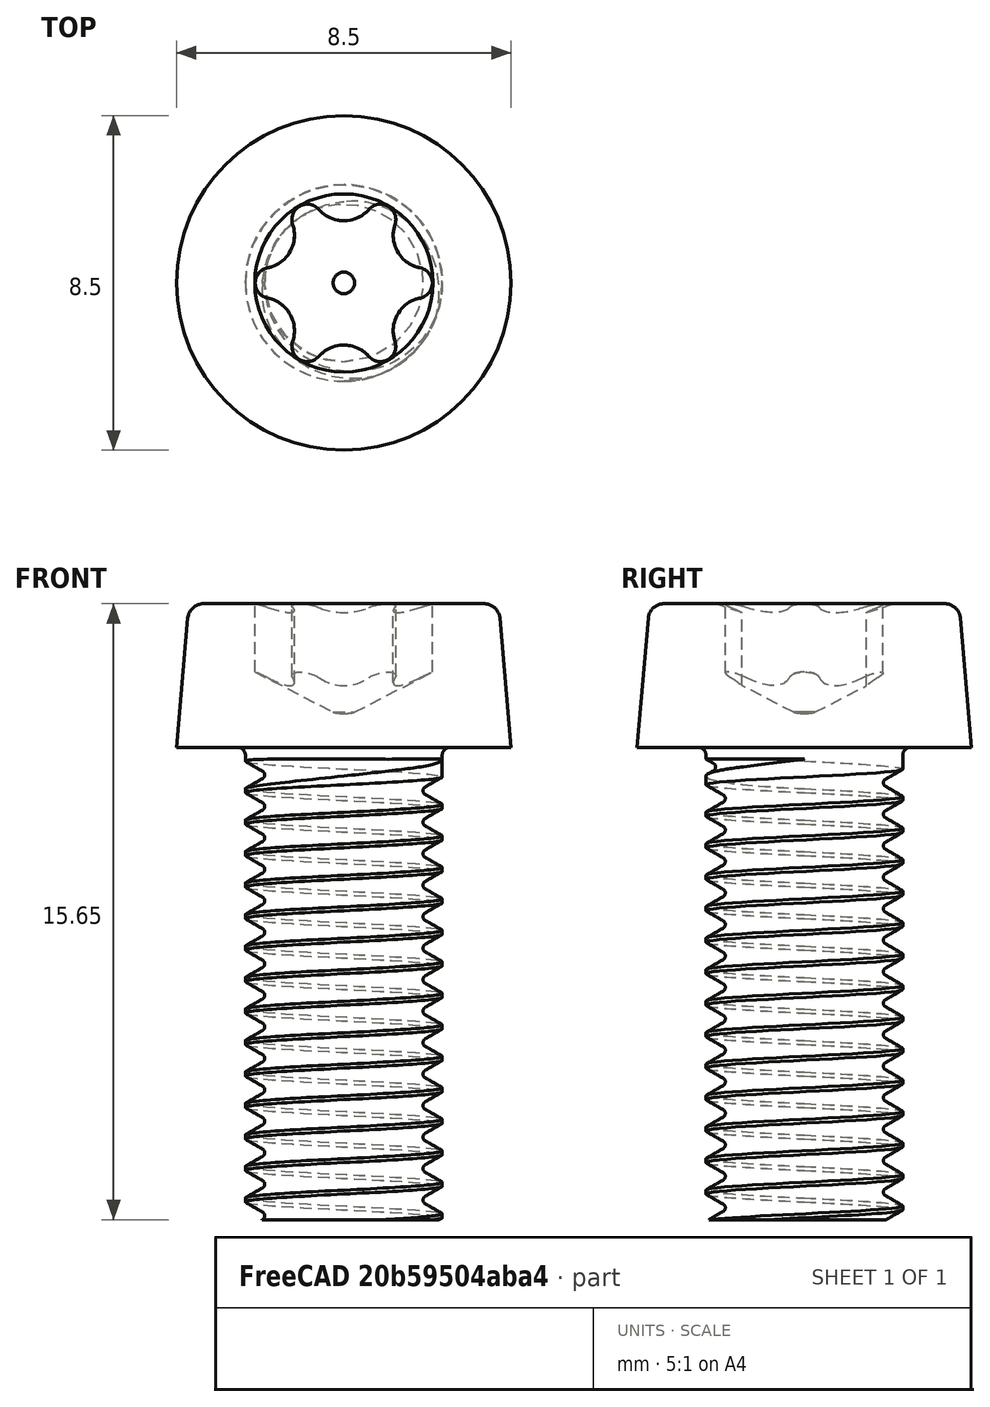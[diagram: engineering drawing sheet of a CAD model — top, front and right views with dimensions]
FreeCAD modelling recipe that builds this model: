
FCSTD DOCUMENT  (FreeCAD 0.20R29410 (Git))
Label: Assembly
License: All rights reserved
LicenseURL: http://en.wikipedia.org/wiki/All_rights_reserved
objects: App::DocumentObjectGroup×3, App::Link×3, Part::FeaturePython×2, PartDesign::CoordinateSystem×1, App::FeaturePython×1, App::Part×1
note: 3 computed .brp shape members not serialized (recipe doc carries the construction recipe); baked Part::Feature solids carry a one-line shape summary decoded from their .brp
EXTERNAL_REF file=Clip.FCStd obj=LCS_Origin
EXTERNAL_REF file=Clip.FCStd obj=Body
EXTERNAL_REF file=Clip.FCStd obj=HoleAxis_1
EXTERNAL_REF file=Rectangle.FCStd obj=HoleAxis_1
EXTERNAL_REF file=Rectangle.FCStd obj=Part

FEATURE [App::DocumentObjectGroup] Parts
FEATURE [PartDesign::CoordinateSystem] LCS_Origin
  AttacherType = Attacher::AttachEngine3D
  MapMode = 2
  Support = -> [X_Axis]
FEATURE [App::DocumentObjectGroup] Constraints
FEATURE [App::FeaturePython] Variables  # WARN: FeaturePython — macro-defined, semantics opaque (R4)
  Type = App::PropertyContainer
FEATURE [App::DocumentObjectGroup] Configurations
FEATURE [App::Link] Clip  label="ClipTop"
  AssemblyType = Part::Link
  AttachedBy = #LCS_Origin
  AttachedTo = Parent Assembly#LCS_Origin
  LinkedObject = -> <external Clip.FCStd>#Body
  SolverId = Asm4EE
  expr: Placement = LCS_Origin.Placement * AttachmentOffset * Clip#LCS_Origin.Placement ^ -1
FEATURE [Part::FeaturePython] Screw  label="M5x12-Screw"  # Fasteners workbench fastener (typed FeaturePython)
  AssemblyType = Part::Link
  AttachedBy = Origin
  AttachedTo = Clip#HoleAxis_1
  Placement = pos=(25,-5,3) rot=(0,0,1;3.14159rad)
  SolverId = Asm4EE
  diameter = 7
  invert = false
  leftHanded = false
  length = 3
  lengthCustom = 12
  matchOuter = false
  offset = 0
  thread = true
  type = 29
  expr: Placement = Clip.Placement * Clip#HoleAxis_1.Placement * AttachmentOffset
FEATURE [App::Link] Rectangle
  AssemblyType = Part::Link
  AttachedBy = #HoleAxis_1
  AttachedTo = Clip#HoleAxis_1
  AttachmentOffset = pos=(0,0,-3) rot=(0,0,1;4.71239rad)
  LinkPlacement = pos=(25,17.5,-3) rot=(0,0,-1;4.71239rad)
  LinkedObject = -> <external Rectangle.FCStd>#Part
  Placement = pos=(25,17.5,-3) rot=(0,0,-1;4.71239rad)
  SolverId = Asm4EE
  expr: Placement = Clip.Placement * Clip#HoleAxis_1.Placement * AttachmentOffset * Rectangle#HoleAxis_1.Placement ^ -1
FEATURE [Part::FeaturePython] Nut  label="M5-Nut"  # Fasteners workbench fastener (typed FeaturePython)
  AssemblyType = Part::Link
  AttachedBy = Origin
  AttachedTo = Clip#HoleAxis_1
  AttachmentOffset = pos=(0,0,-12) rot=(0,0,1;0rad)
  Placement = pos=(25,-5,-9) rot=(0,0,1;3.14159rad)
  SolverId = Asm4EE
  diameter = 7
  invert = false
  leftHanded = false
  matchOuter = false
  offset = 0
  thread = true
  type = 12
  expr: Placement = Clip.Placement * Clip#HoleAxis_1.Placement * AttachmentOffset
FEATURE [App::Link] ClipBottom
  AssemblyType = Part::Link
  AttachedBy = #HoleAxis_1
  AttachedTo = Clip#HoleAxis_1
  AttachmentOffset = pos=(0,0,-9) rot=(1,0,0;3.14159rad)
  LinkPlacement = pos=(0,-10,-3) rot=(-1,0,0;3.14159rad)
  LinkedObject = -> <external Clip.FCStd>#Body
  Placement = pos=(0,-10,-3) rot=(-1,0,0;3.14159rad)
  SolverId = Asm4EE
  expr: Placement = Clip.Placement * Clip#HoleAxis_1.Placement * AttachmentOffset * Clip#HoleAxis_1.Placement ^ -1
FEATURE [App::Part] Model
  AssemblyType = Part::Link
  Group = -> [LCS_Origin,Constraints,Variables,Configurations,Clip,Screw,Rectangle,Nut,ClipBottom]
  Origin = -> Origin
  Type = Assembly

RESOLVED EXTERNAL PARTS (link-assembly join: the EXTERNAL_REF files above that resolve inside this repo's crawl, each included once):
---- part Clip.FCStd = doc fcstd_39144fcac201 ----
FCSTD DOCUMENT  (FreeCAD 0.20R29410 (Git))
Label: Clip
License: All rights reserved
LicenseURL: http://en.wikipedia.org/wiki/All_rights_reserved
objects: Sketcher::SketchObject×2, PartDesign::Pad×1, PartDesign::Pocket×1, PartDesign::CoordinateSystem×1, PartDesign::Line×1, PartDesign::Body×1
note: 9 computed .brp shape members not serialized (recipe doc carries the construction recipe); baked Part::Feature solids carry a one-line shape summary decoded from their .brp

FEATURE [Sketcher::SketchObject] Sketch
  FullyConstrained = true
  MapMode = 5
  Placement = pos=(0,0,0) rot=(1,0,0;1.5708rad)
  Support = -> [XZ_Plane]
  sketch-geometry (10):
    g0: LineSegment StartX=-30 StartY=0 StartZ=0 EndX=-17 EndY=0 EndZ=0
    g1: ArcOfCircle CenterX=0 CenterY=0 CenterZ=0 NormalX=0 NormalY=0 NormalZ=1 AngleXU=0 Radius=20.2237 StartAngle=0.14889 EndAngle=2.9927
    g2: LineSegment StartX=-30 StartY=0 StartZ=0 EndX=-30 EndY=3 EndZ=0
    g3: LineSegment StartX=-30 StartY=3 StartZ=0 EndX=-20 EndY=3 EndZ=0
    g4: LineSegment StartX=30 StartY=0 StartZ=0 EndX=30 EndY=3 EndZ=0
    g5: LineSegment StartX=30 StartY=3 StartZ=0 EndX=20 EndY=3 EndZ=0
    g6: ArcOfCircle CenterX=0 CenterY=0 CenterZ=0 NormalX=0 NormalY=0 NormalZ=1 AngleXU=0 Radius=17.2627 StartAngle=0.174672 EndAngle=2.96692
    g7: LineSegment StartX=-17 StartY=3 StartZ=0 EndX=-17 EndY=0 EndZ=0
    g8: LineSegment StartX=17 StartY=3 StartZ=0 EndX=17 EndY=0 EndZ=0
    g9: LineSegment StartX=17 StartY=0 StartZ=0 EndX=30 EndY=0 EndZ=0
  constraints (29):
    c: PointOnObject(g0,g-1)
    c: PointOnObject(g9,g-1)
    c: Coincident(g0,g2)
    c: Coincident(g2,g3)
    c: Coincident(g3,g1)
    c: Coincident(g9,g4)
    c: Coincident(g4,g5)
    c: Coincident(g5,g1)
    c: Horizontal(g5)
    c: Vertical(g2)
    c: Vertical(g4)
    c: Horizontal(g3)
    c: Equal(g3,g5)
    c: Equal(g2,g4)
    c: DistanceX(g5,g5) = 10
    c: DistanceX(g0,g9) = 60
    c: DistanceY(g4,g4) = 3
    c: Coincident(g1,g-1)
    c: Horizontal(g1,g6)
    c: Horizontal(g6,g6)
    c: Coincident(g7,g6)
    c: Vertical(g7)
    c: Coincident(g8,g6)
    c: DistanceX(g1,g6) = 3
    c: Coincident(g6,g1)
    c: Coincident(g0,g7)
    c: Coincident(g9,g8)
    c: Symmetric(g0,g8,g1)
    c: PointOnObject(g8,g-1)
FEATURE [PartDesign::Pad] Pad
  Direction = (0,-1,2e-16)
  Length = 10
  Length2 = 10
  Placement = pos=(0,0,0) rot=(1,0,0;1.5708rad)
  Profile = -> Sketch
  ReferenceAxis = -> Sketch [N_Axis]
  Type = 0
FEATURE [Sketcher::SketchObject] Sketch001
  ExternalGeometry = -> [Pad]
  FullyConstrained = true
  MapMode = 5
  Placement = pos=(0,2e-15,3) rot=(0,0,1;3.14159rad)
  Support = -> [Pad]
  sketch-geometry (2):
    g0: Circle CenterX=-25 CenterY=5 CenterZ=0 NormalX=0 NormalY=0 NormalZ=1 AngleXU=0 Radius=2.5
    g1: Circle CenterX=25 CenterY=5 CenterZ=0 NormalX=0 NormalY=0 NormalZ=1 AngleXU=0 Radius=2.5
  constraints (4):
    c: Symmetric(g0,g1,g-2)
    c: Symmetric(g-3,g-5,g0)
    c: Equal(g0,g1)
    c: Diameter(g0) = 5
FEATURE [PartDesign::Pocket] Pocket
  BaseFeature = -> Pad
  Direction = (0,-2e-16,-1)
  Length = 5
  Length2 = 5
  Placement = pos=(0,0,0) rot=(1,0,0;1.5708rad)
  Profile = -> Sketch001
  ReferenceAxis = -> Sketch001 [N_Axis]
  Type = 1
FEATURE [PartDesign::CoordinateSystem] LCS_Origin
  AttacherType = Attacher::AttachEngine3D
  Support = -> [Pocket]
FEATURE [PartDesign::Line] HoleAxis_1
  AttacherType = Attacher::AttachEngineLine
  Length = 7.04534
  MapMode = 19
  Placement = pos=(25,-5,3) rot=(0,0,1;3.14159rad)
  ResizeMode = 1
  Support = -> [Pocket]
FEATURE [PartDesign::Body] Body
  Group = -> [Sketch,Pad,Sketch001,Pocket,LCS_Origin,HoleAxis_1]
  Origin = -> Origin
  Tip = -> Pocket
---- part Rectangle.FCStd = doc fcstd_1559d51382fe ----
FCSTD DOCUMENT  (FreeCAD 0.20R29410 (Git))
Label: Rectangle
License: All rights reserved
LicenseURL: http://en.wikipedia.org/wiki/All_rights_reserved
objects: Sketcher::SketchObject×1, Part::Extrusion×1, PartDesign::Line×1, App::Part×1
note: 3 computed .brp shape members not serialized (recipe doc carries the construction recipe); baked Part::Feature solids carry a one-line shape summary decoded from their .brp

FEATURE [Sketcher::SketchObject] Sketch
  FullyConstrained = true
  sketch-geometry (5):
    g0: LineSegment StartX=-27.5 StartY=5 StartZ=0 EndX=27.5 EndY=5 EndZ=0
    g1: LineSegment StartX=27.5 StartY=5 StartZ=0 EndX=27.5 EndY=-5 EndZ=0
    g2: LineSegment StartX=27.5 StartY=-5 StartZ=0 EndX=-27.5 EndY=-5 EndZ=0
    g3: LineSegment StartX=-27.5 StartY=-5 StartZ=0 EndX=-27.5 EndY=5 EndZ=0
    g4: Circle CenterX=-22.5 CenterY=0 CenterZ=0 NormalX=0 NormalY=0 NormalZ=1 AngleXU=0 Radius=2.5
  constraints (14):
    c: Coincident(g0,g1)
    c: Coincident(g1,g2)
    c: Coincident(g2,g3)
    c: Coincident(g3,g0)
    c: Horizontal(g0)
    c: Horizontal(g2)
    c: Vertical(g1)
    c: Vertical(g3)
    c: Symmetric(g0,g2,g-1)
    c: DistanceX(g0,g0) = 55
    c: DistanceY(g1,g1) = 10
    c: Diameter(g4) = 5
    c: DistanceX(g0,g4) = 5
    c: PointOnObject(g4,g-1)
FEATURE [Part::Extrusion] Extrude
  Base = -> Sketch
  Dir = (0,0,1)
  DirMode = 2
  FaceMakerClass = Part::FaceMakerBullseye
  LengthFwd = 3
  LengthRev = 0
  Solid = true
  Symmetric = false
FEATURE [PartDesign::Line] HoleAxis_1
  AttacherType = Attacher::AttachEngineLine
  Length = 7.04534
  MapMode = 19
  Placement = pos=(-22.5,0,3) rot=(0,0,1;0rad)
  ResizeMode = 1
  Support = -> [Extrude]
FEATURE [App::Part] Part  label="RectanglePart"
  Group = -> [Sketch,Extrude,HoleAxis_1]
  Origin = -> Origin
